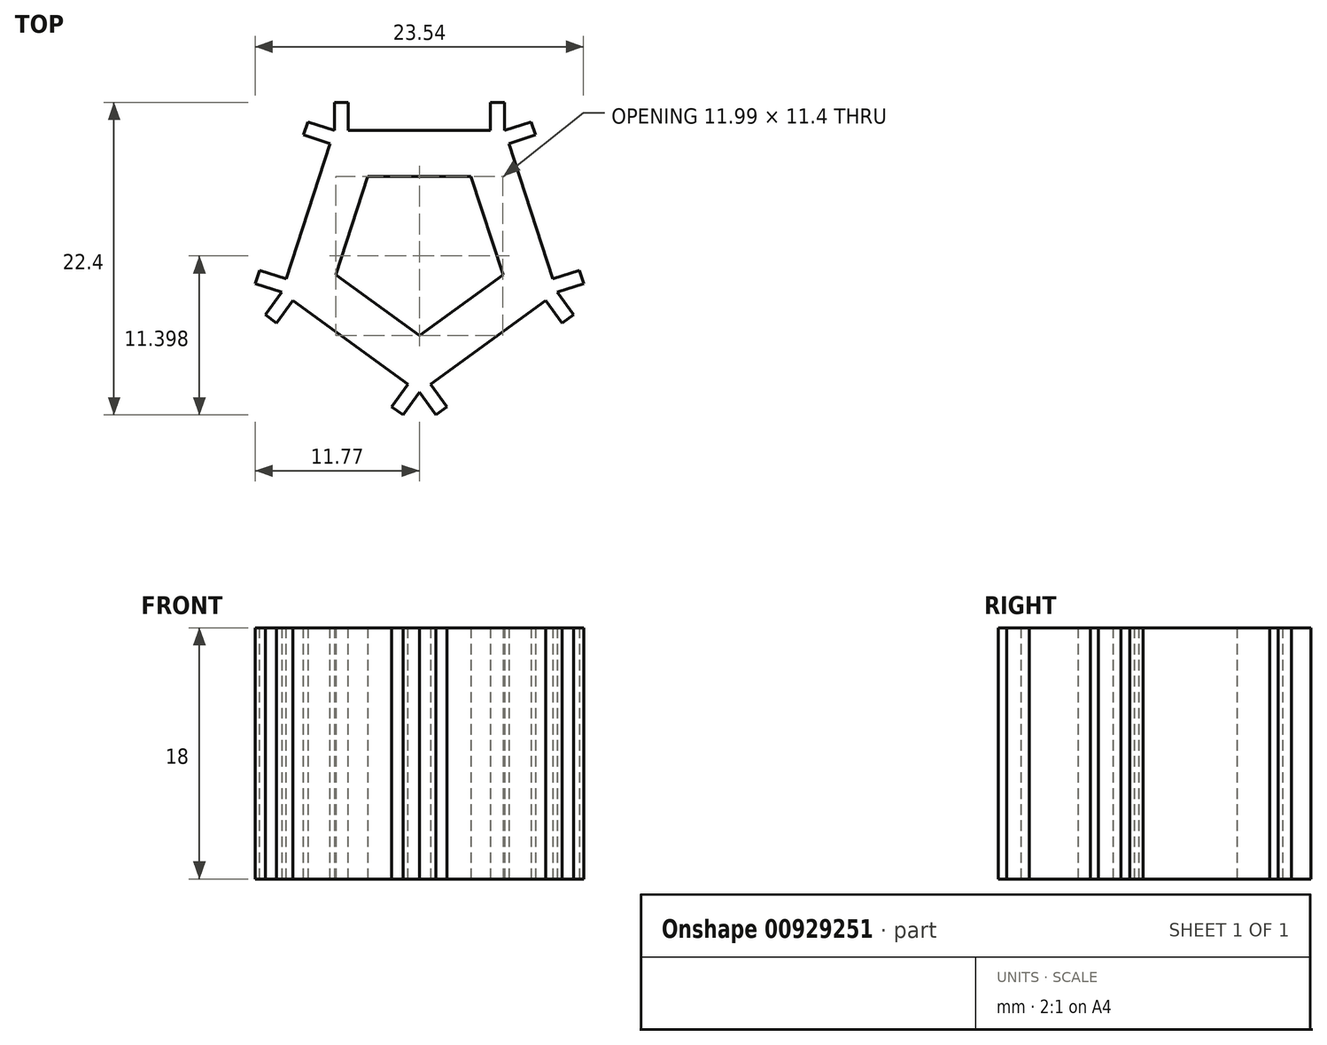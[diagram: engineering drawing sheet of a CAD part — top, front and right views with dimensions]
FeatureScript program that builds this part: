
annotation { "Feature Type Name" : "Feature", "Feature Type Description" : "" }
export const myFeature = defineFeature(function(context is Context, id is Id, definition is map)
    precondition{}
    {
        {
            var Q0;
            Q0=qCreatedBy(makeId("Top.planeOp"),FACE);
            var sketch = newSketch(context, id + "F0", { "sketchPlane" : qUnion([Q0])});
            skCircle(sketch, "E0.cCircle", {"center": v(0, 0) * mm, "radius": 5.1 * mm, "construction": true});
            skLineSegment(sketch, "E0.0", {"start": v(-3.7, 5.1) * mm, "end": v(3.7, 5.1) * mm});
            skLineSegment(sketch, "E0.1", {"start": v(3.7, 5.1) * mm, "end": v(6, -1.95) * mm});
            skLineSegment(sketch, "E0.2", {"start": v(6, -1.95) * mm, "end": v(0, -6.3) * mm});
            skLineSegment(sketch, "E0.3", {"start": v(0, -6.3) * mm, "end": v(-6, -1.95) * mm});
            skLineSegment(sketch, "E0.4", {"start": v(-6, -1.95) * mm, "end": v(-3.7, 5.1) * mm});
            skPoint(sketch, "E0.0.midPoint", {"position": v(0, 5.1) * mm});
            skLineSegment(sketch, "E1.0", {"start": v(9.87, -3.2) * mm, "end": v(0, -10.38) * mm});
            skLineSegment(sketch, "E1.1", {"start": v(6.1, 8.4) * mm, "end": v(9.87, -3.2) * mm});
            skLineSegment(sketch, "E1.2", {"start": v(0, -10.38) * mm, "end": v(-9.87, -3.2) * mm});
            skLineSegment(sketch, "E1.3", {"start": v(-9.87, -3.2) * mm, "end": v(-6.1, 8.4) * mm});
            skLineSegment(sketch, "E1.4", {"start": v(-6.1, 8.4) * mm, "end": v(6.1, 8.4) * mm});
            skSolve(sketch);
        }
        {
            var Q0;
            Q0=makeQuery(id+"F0.imprint","IMPRINT",FACE,{"disambiguationData":[TD([[makeQuery(id+"F0.imprint","IMPRINT",EDGE,{"derivedFrom":sQuery(id+"F0.wireOp",EDGE,"E0.0")}),1.0]])]});
            extrude(context, id + "F1", {"entities" : qUnion([Q0]), "depth" : 18 * mm, "offsetDistance" : 25 * mm});
        }
        {
            var Q0;
            Q0=makeQuery(id+"F1.opExtrude","SWEPT_FACE",FACE,{"disambiguationData":[OSD([sQuery(id+"F0.wireOp",EDGE,"E1.0")])]});
            var sketch = newSketch(context, id + "F2", { "sketchPlane" : qUnion([Q0])});
            skPoint(sketch, "E2", {"position": v(-6.1, 18) * mm});
            skPoint(sketch, "E3", {"position": v(6.1, 18) * mm});
            skPoint(sketch, "E4", {"position": v(6.1, 0) * mm});
            skPoint(sketch, "E5", {"position": v(-6.1, 0) * mm});
            skLineSegment(sketch, "E6.bottom", {"start": v(-6.1, 18) * mm, "end": v(-5.1, 18) * mm});
            skLineSegment(sketch, "E6.top", {"start": v(-6.1, 0) * mm, "end": v(-5.1, 0) * mm});
            skLineSegment(sketch, "E6.left", {"start": v(-6.1, 18) * mm, "end": v(-6.1, 0) * mm});
            skLineSegment(sketch, "E6.right", {"start": v(-5.1, 18) * mm, "end": v(-5.1, 0) * mm});
            skLineSegment(sketch, "E7.bottom", {"start": v(6.1, 18) * mm, "end": v(5.1, 18) * mm});
            skLineSegment(sketch, "E7.top", {"start": v(6.1, 0) * mm, "end": v(5.1, 0) * mm});
            skLineSegment(sketch, "E7.left", {"start": v(6.1, 18) * mm, "end": v(6.1, 0) * mm});
            skLineSegment(sketch, "E7.right", {"start": v(5.1, 18) * mm, "end": v(5.1, 0) * mm});
            skSolve(sketch);
        }
        {
            var Q0;
            Q0=makeQuery(id+"F2.imprint","IMPRINT",FACE,{"disambiguationData":[TD([[makeQuery(id+"F2.imprint","IMPRINT",EDGE,{"derivedFrom":sQuery(id+"F2.wireOp",EDGE,"E6.bottom")}),1.0]])]});
            var Q1;
            Q1=makeQuery(id+"F2.imprint","IMPRINT",FACE,{"disambiguationData":[TD([[makeQuery(id+"F2.imprint","IMPRINT",EDGE,{"derivedFrom":sQuery(id+"F2.wireOp",EDGE,"E7.bottom")}),1.0]])]});
            extrude(context, id + "F3", {"entities" : qUnion([Q0, Q1]), "operationType" : NewBodyOperationType.ADD, "depth" : 2 * mm, "offsetDistance" : 25 * mm});
        }
        {
            var Q0;
            Q0=makeQuery(id+"F1.opExtrude","SWEPT_FACE",FACE,{"disambiguationData":[OSD([sQuery(id+"F0.wireOp",EDGE,"E1.2")])]});
            var sketch = newSketch(context, id + "F4", { "sketchPlane" : qUnion([Q0])});
            skPoint(sketch, "E8", {"position": v(-6.1, 18) * mm});
            skPoint(sketch, "E9", {"position": v(6.1, 18) * mm});
            skPoint(sketch, "E10", {"position": v(6.1, 0) * mm});
            skPoint(sketch, "E11", {"position": v(-6.1, 0) * mm});
            skLineSegment(sketch, "E12.bottom", {"start": v(-6.1, 18) * mm, "end": v(-5.1, 18) * mm});
            skLineSegment(sketch, "E12.top", {"start": v(-6.1, 0) * mm, "end": v(-5.1, 0) * mm});
            skLineSegment(sketch, "E12.left", {"start": v(-6.1, 18) * mm, "end": v(-6.1, 0) * mm});
            skLineSegment(sketch, "E12.right", {"start": v(-5.1, 18) * mm, "end": v(-5.1, 0) * mm});
            skLineSegment(sketch, "E13.bottom", {"start": v(6.1, 0) * mm, "end": v(5.1, 0) * mm});
            skLineSegment(sketch, "E13.top", {"start": v(6.1, 18) * mm, "end": v(5.1, 18) * mm});
            skLineSegment(sketch, "E13.left", {"start": v(6.1, 0) * mm, "end": v(6.1, 18) * mm});
            skLineSegment(sketch, "E13.right", {"start": v(5.1, 0) * mm, "end": v(5.1, 18) * mm});
            skSolve(sketch);
        }
        {
            var Q0;
            Q0=makeQuery(id+"F4.imprint","IMPRINT",FACE,{"disambiguationData":[TD([[makeQuery(id+"F4.imprint","IMPRINT",EDGE,{"derivedFrom":sQuery(id+"F4.wireOp",EDGE,"E13.bottom")}),-1.0]])]});
            var Q1;
            Q1=makeQuery(id+"F4.imprint","IMPRINT",FACE,{"disambiguationData":[TD([[makeQuery(id+"F4.imprint","IMPRINT",EDGE,{"derivedFrom":sQuery(id+"F4.wireOp",EDGE,"E12.bottom")}),1.0]])]});
            extrude(context, id + "F5", {"entities" : qUnion([Q0, Q1]), "operationType" : NewBodyOperationType.ADD, "depth" : 2 * mm, "offsetDistance" : 25 * mm});
        }
        {
            var Q0;
            Q0=makeQuery(id+"F1.opExtrude","SWEPT_FACE",FACE,{"disambiguationData":[OSD([sQuery(id+"F0.wireOp",EDGE,"E1.3")])]});
            var sketch = newSketch(context, id + "F6", { "sketchPlane" : qUnion([Q0])});
            skPoint(sketch, "E14", {"position": v(6.1, 0) * mm});
            skPoint(sketch, "E15", {"position": v(6.1, 18) * mm});
            skPoint(sketch, "E16", {"position": v(-6.1, 18) * mm});
            skPoint(sketch, "E17", {"position": v(-6.1, 0) * mm});
            skLineSegment(sketch, "E18.bottom", {"start": v(6.1, 0) * mm, "end": v(5.1, 0) * mm});
            skLineSegment(sketch, "E18.top", {"start": v(6.1, 18) * mm, "end": v(5.1, 18) * mm});
            skLineSegment(sketch, "E18.left", {"start": v(6.1, 0) * mm, "end": v(6.1, 18) * mm});
            skLineSegment(sketch, "E18.right", {"start": v(5.1, 0) * mm, "end": v(5.1, 18) * mm});
            skLineSegment(sketch, "E19.bottom", {"start": v(-6.1, 0) * mm, "end": v(-5.1, 0) * mm});
            skLineSegment(sketch, "E19.top", {"start": v(-6.1, 18) * mm, "end": v(-5.1, 18) * mm});
            skLineSegment(sketch, "E19.left", {"start": v(-6.1, 0) * mm, "end": v(-6.1, 18) * mm});
            skLineSegment(sketch, "E19.right", {"start": v(-5.1, 0) * mm, "end": v(-5.1, 18) * mm});
            skSolve(sketch);
        }
        {
            var Q0;
            Q0=makeQuery(id+"F6.imprint","IMPRINT",FACE,{"disambiguationData":[TD([[makeQuery(id+"F6.imprint","IMPRINT",EDGE,{"derivedFrom":sQuery(id+"F6.wireOp",EDGE,"E18.bottom")}),-1.0]])]});
            var Q1;
            Q1=makeQuery(id+"F6.imprint","IMPRINT",FACE,{"disambiguationData":[TD([[makeQuery(id+"F6.imprint","IMPRINT",EDGE,{"derivedFrom":sQuery(id+"F6.wireOp",EDGE,"E19.bottom")}),-1.0]])]});
            extrude(context, id + "F7", {"entities" : qUnion([Q0, Q1]), "operationType" : NewBodyOperationType.ADD, "depth" : 2 * mm, "offsetDistance" : 25 * mm});
        }
        {
            var Q0;
            Q0=makeQuery(id+"F1.opExtrude","SWEPT_FACE",FACE,{"disambiguationData":[OSD([sQuery(id+"F0.wireOp",EDGE,"E1.1")])]});
            var sketch = newSketch(context, id + "F8", { "sketchPlane" : qUnion([Q0])});
            skPoint(sketch, "E20", {"position": v(-6.1, 18) * mm});
            skPoint(sketch, "E21", {"position": v(6.1, 18) * mm});
            skPoint(sketch, "E22", {"position": v(6.1, 0) * mm});
            skPoint(sketch, "E23", {"position": v(-6.1, 0) * mm});
            skLineSegment(sketch, "E24.bottom", {"start": v(-6.1, 18) * mm, "end": v(-5.1, 18) * mm});
            skLineSegment(sketch, "E24.top", {"start": v(-6.1, 0) * mm, "end": v(-5.1, 0) * mm});
            skLineSegment(sketch, "E24.left", {"start": v(-6.1, 18) * mm, "end": v(-6.1, 0) * mm});
            skLineSegment(sketch, "E24.right", {"start": v(-5.1, 18) * mm, "end": v(-5.1, 0) * mm});
            skLineSegment(sketch, "E25.bottom", {"start": v(6.1, 18) * mm, "end": v(5.1, 18) * mm});
            skLineSegment(sketch, "E25.top", {"start": v(6.1, 0) * mm, "end": v(5.1, 0) * mm});
            skLineSegment(sketch, "E25.left", {"start": v(6.1, 18) * mm, "end": v(6.1, 0) * mm});
            skLineSegment(sketch, "E25.right", {"start": v(5.1, 18) * mm, "end": v(5.1, 0) * mm});
            skSolve(sketch);
        }
        {
            var Q0;
            Q0=makeQuery(id+"F8.imprint","IMPRINT",FACE,{"disambiguationData":[TD([[makeQuery(id+"F8.imprint","IMPRINT",EDGE,{"derivedFrom":sQuery(id+"F8.wireOp",EDGE,"E24.bottom")}),1.0]])]});
            var Q1;
            Q1=makeQuery(id+"F8.imprint","IMPRINT",FACE,{"disambiguationData":[TD([[makeQuery(id+"F8.imprint","IMPRINT",EDGE,{"derivedFrom":sQuery(id+"F8.wireOp",EDGE,"E25.bottom")}),1.0]])]});
            extrude(context, id + "F9", {"entities" : qUnion([Q0, Q1]), "operationType" : NewBodyOperationType.ADD, "depth" : 2 * mm, "offsetDistance" : 25 * mm});
        }
        {
            var Q0;
            Q0=makeQuery(id+"F1.opExtrude","SWEPT_FACE",FACE,{"disambiguationData":[OSD([sQuery(id+"F0.wireOp",EDGE,"E1.4")])]});
            var sketch = newSketch(context, id + "F10", { "sketchPlane" : qUnion([Q0])});
            skPoint(sketch, "E26", {"position": v(6.1, 18) * mm});
            skPoint(sketch, "E27", {"position": v(-6.1, 18) * mm});
            skPoint(sketch, "E28", {"position": v(6.1, 0) * mm});
            skPoint(sketch, "E29", {"position": v(-6.1, 0) * mm});
            skLineSegment(sketch, "E30.bottom", {"start": v(-6.1, 18) * mm, "end": v(-5.1, 18) * mm});
            skLineSegment(sketch, "E30.top", {"start": v(-6.1, 0) * mm, "end": v(-5.1, 0) * mm});
            skLineSegment(sketch, "E30.left", {"start": v(-6.1, 18) * mm, "end": v(-6.1, 0) * mm});
            skLineSegment(sketch, "E30.right", {"start": v(-5.1, 18) * mm, "end": v(-5.1, 0) * mm});
            skLineSegment(sketch, "E31.bottom", {"start": v(6.1, 0) * mm, "end": v(5.1, 0) * mm});
            skLineSegment(sketch, "E31.top", {"start": v(6.1, 18) * mm, "end": v(5.1, 18) * mm});
            skLineSegment(sketch, "E31.left", {"start": v(6.1, 0) * mm, "end": v(6.1, 18) * mm});
            skLineSegment(sketch, "E31.right", {"start": v(5.1, 0) * mm, "end": v(5.1, 18) * mm});
            skSolve(sketch);
        }
        {
            var Q0;
            Q0=makeQuery(id+"F10.imprint","IMPRINT",FACE,{"disambiguationData":[TD([[makeQuery(id+"F10.imprint","IMPRINT",EDGE,{"derivedFrom":sQuery(id+"F10.wireOp",EDGE,"E31.bottom")}),-1.0]])]});
            var Q1;
            Q1=makeQuery(id+"F10.imprint","IMPRINT",FACE,{"disambiguationData":[TD([[makeQuery(id+"F10.imprint","IMPRINT",EDGE,{"derivedFrom":sQuery(id+"F10.wireOp",EDGE,"E30.bottom")}),1.0]])]});
            extrude(context, id + "F11", {"entities" : qUnion([Q0, Q1]), "operationType" : NewBodyOperationType.ADD, "depth" : 2 * mm, "offsetDistance" : 25 * mm});
        }
    });
